# Revit family: Faucet-Kitchen-Grohe-K7-32951_Series
name_source: partatom
category: Plumbing Fixtures
revit_build: Autodesk Revit 2014 (Build: 20130308_1515(x64)
units: mm (PartAtom-declared; Revit-internal decimal feet)

## types (2) — shared parameters
ADA Compliant = Yes
Assembly Code = D2020300
CW Connection = Yes
CWFU = 1.5
CalGreen Compliant = Yes
Cold Water Connection Diameter = 3/8"
Default Elevation = 0"
Description = K7 Semi-Pro Faucet Single-lever sink mixer 1/2"
Flow Rate = 1.75 gpm (6.6 L/min)
HW Connection = Yes
HWFU = 1.5
Height = 26 9/16"
Hot Water Connection Diameter = 0"
Installation Type = Deck-Mounted
Length = 9 3/16"
Manufacturer = Grohe
Price = Prices may vary. Please consult Manufacturer Representative for most up-to-date price list.
Product Page URL = https://www.grohe.com
Shipping Weight = 11.43 lb
URL = http://www.grohe.com
Vent Connection = No
Warranty Documentation Link = https://cdn.cloud.grohe.com
Waste Connection = No
cUPC Compliant = Yes
zero-valued in all types: WFU

## per-type parameters (varying)
| type | Finish | Material |
| 32951000 | Metal-Grohe-000-Chrome | Metal-Grohe-000-Chrome |
| 32951DC0 | Metal-Grohe-DC0-Stainless Steel | Metal-Grohe-DC0-Stainless Steel |

note: column(s) folded — value = type name in every type: Model
